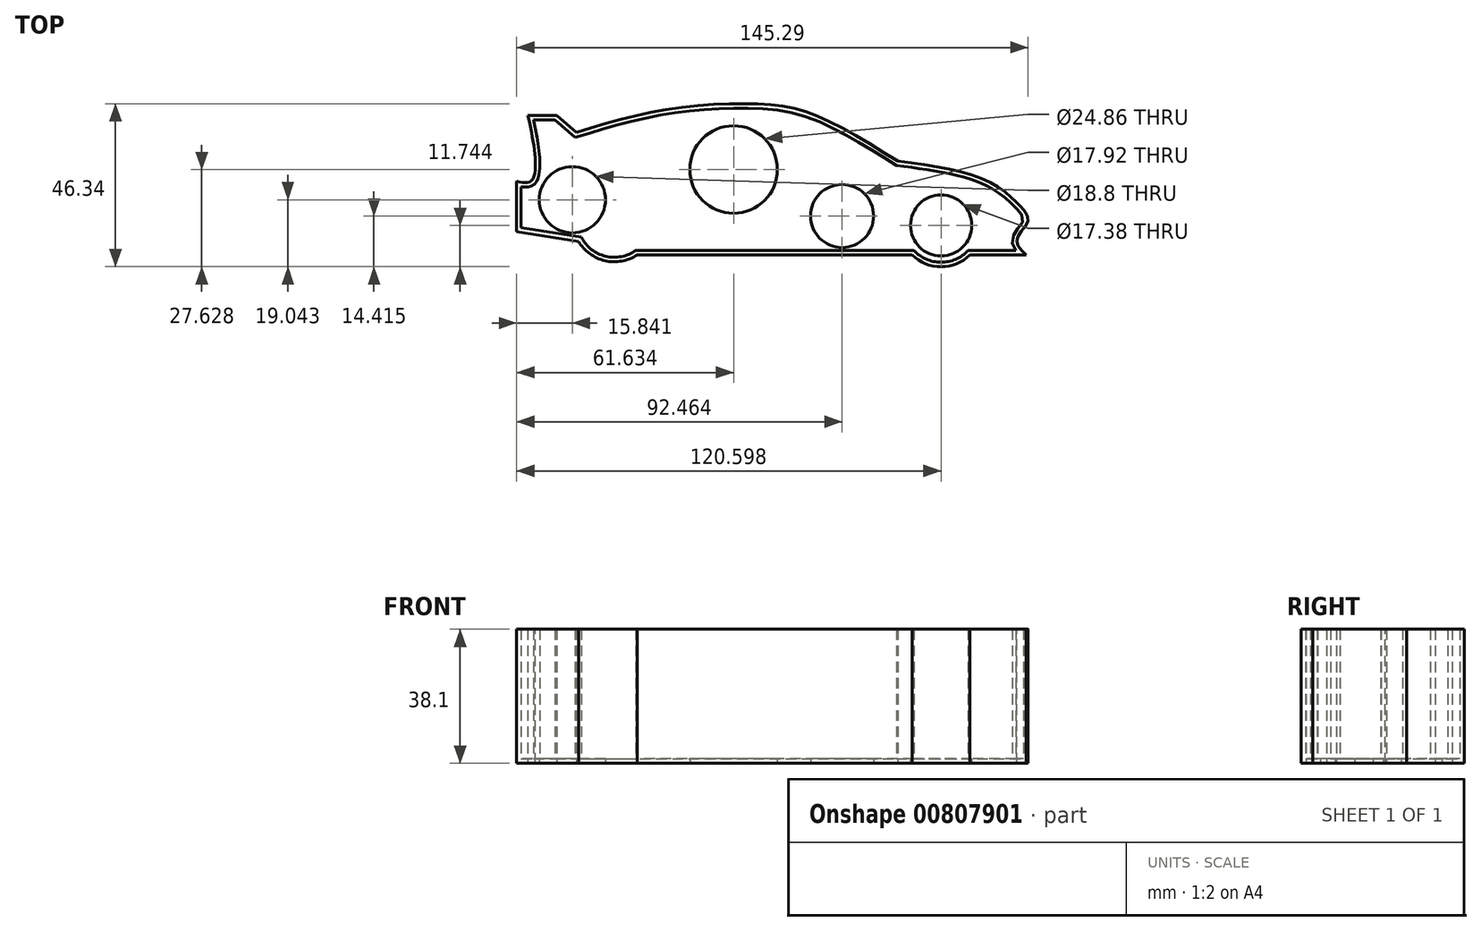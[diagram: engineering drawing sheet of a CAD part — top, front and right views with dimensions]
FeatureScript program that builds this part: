
annotation { "Feature Type Name" : "Feature", "Feature Type Description" : "" }
export const myFeature = defineFeature(function(context is Context, id is Id, definition is map)
    precondition{}
    {
        {
            var Q0;
            Q0=qCreatedBy(makeId("Top.planeOp"),FACE);
            var sketch = newSketch(context, id + "F0", { "sketchPlane" : qUnion([Q0])});
            skFitSpline(sketch, "E0", {"points": [v(35.9, -3.78) * mm, v(61.02, -9.28) * mm, v(70.44, -16.34) * mm, v(72.8, -20.8) * mm, v(69.66, -26.02) * mm, v(72.27, -30.47) * mm], "startDerivative": vector(86.14, -11.78) * mm, "endDerivative": vector(29.8, -29.47) * mm});
            skLineSegment(sketch, "E1", {"start": v(72.27, -30.47) * mm, "end": v(56.34, -30.47) * mm});
            skLineSegment(sketch, "E2", {"start": v(39.86, -30.4) * mm, "end": v(39.86, -30.4) * mm});
            skLineSegment(sketch, "E3", {"start": v(-54.84, -26.57) * mm, "end": v(-72.43, -23.8) * mm});
            skLineSegment(sketch, "E4", {"start": v(-72.43, -23.8) * mm, "end": v(-72.43, -9.5) * mm});
            skFitSpline(sketch, "E5", {"points": [v(-72.43, -9.5) * mm, v(-68.34, -9.5) * mm, v(-67.18, -2.77) * mm, v(-69.22, 9.2) * mm], "startDerivative": vector(18.96, -4.5) * mm, "endDerivative": vector(-6.22, 28.23) * mm});
            skLineSegment(sketch, "E6", {"start": v(-69.22, 9.2) * mm, "end": v(-61.04, 9.2) * mm});
            skLineSegment(sketch, "E7", {"start": v(-61.04, 9.2) * mm, "end": v(-55.49, 4.38) * mm});
            skFitSpline(sketch, "E8", {"points": [v(-55.49, 4.38) * mm, v(-29.5, 10.95) * mm, v(-3.23, 12.41) * mm, v(12.54, 9.2) * mm, v(35.9, -3.78) * mm], "startDerivative": vector(95.2, 28.83) * mm, "endDerivative": vector(93.12, -57.68) * mm});
            skArc(sketch, "E9", {"start": v(-54.84, -26.57) * mm, "mid": v(-47.33, -32.07) * mm, "end": v(-38.17, -30.4) * mm});
            skLineSegment(sketch, "E10", {"start": v(39.92, -30.4) * mm, "end": v(-38.17, -30.4) * mm});
            skArc(sketch, "E11", {"start": v(39.92, -30.4) * mm, "mid": v(48.12, -33.79) * mm, "end": v(56.34, -30.47) * mm});
            skSolve(sketch);
        }
        {
            var Q0;
            Q0=makeQuery(id+"F0.imprint","IMPRINT",FACE,{"disambiguationData":[TD([[makeQuery(id+"F0.imprint","IMPRINT",EDGE,{"derivedFrom":sQuery(id+"F0.wireOp",EDGE,"E0")}),-1.0]])]});
            extrude(context, id + "F1", {"entities" : qUnion([Q0]), "depth" : 38.1 * mm, "offsetDistance" : 25.4 * mm});
        }
        {
            var Q0;
            Q0=makeQuery(id+"F1.opExtrude","CAP_FACE",FACE,{"disambiguationData":[OSD([sQuery(id+"F0.wireOp",EDGE,"E0"),sQuery(id+"F0.wireOp",EDGE,"E1"),sQuery(id+"F0.wireOp",EDGE,"E3"),sQuery(id+"F0.wireOp",EDGE,"E4"),sQuery(id+"F0.wireOp",EDGE,"E5"),sQuery(id+"F0.wireOp",EDGE,"E6"),sQuery(id+"F0.wireOp",EDGE,"E7"),sQuery(id+"F0.wireOp",EDGE,"E8"),sQuery(id+"F0.wireOp",EDGE,"E9"),sQuery(id+"F0.wireOp",EDGE,"E10"),sQuery(id+"F0.wireOp",EDGE,"E11")])],"isStart":false});
            shell(context, id + "F2", {"entities" : qUnion([Q0]), "thickness" : 1.27 * mm});
        }
        {
            var Q0;
            Q0=makeQuery(id+"F1.opExtrude","CAP_FACE",FACE,{"disambiguationData":[OSD([sQuery(id+"F0.wireOp",EDGE,"E0"),sQuery(id+"F0.wireOp",EDGE,"E1"),sQuery(id+"F0.wireOp",EDGE,"E3"),sQuery(id+"F0.wireOp",EDGE,"E4"),sQuery(id+"F0.wireOp",EDGE,"E5"),sQuery(id+"F0.wireOp",EDGE,"E6"),sQuery(id+"F0.wireOp",EDGE,"E7"),sQuery(id+"F0.wireOp",EDGE,"E8"),sQuery(id+"F0.wireOp",EDGE,"E9"),sQuery(id+"F0.wireOp",EDGE,"E10"),sQuery(id+"F0.wireOp",EDGE,"E11")])],"isStart":true});
            var sketch = newSketch(context, id + "F3", { "sketchPlane" : qUnion([Q0])});
            skCircle(sketch, "E12", {"center": v(-10.8, 6.16) * mm, "radius": 12.43 * mm});
            skCircle(sketch, "E13", {"center": v(20.03, 19.37) * mm, "radius": 8.96 * mm});
            skCircle(sketch, "E14", {"center": v(-56.59, 14.75) * mm, "radius": 9.4 * mm});
            skCircle(sketch, "E15", {"center": v(48.17, 22.05) * mm, "radius": 8.7 * mm});
            skSolve(sketch);
        }
        {
            var Q0;
            Q0 = qSketchRegion(id + "F3", true);
            extrude(context, id + "F4", {"entities" : qUnion([Q0]), "operationType" : NewBodyOperationType.REMOVE, "oppositeDirection" : true, "depth" : 25.4 * mm, "offsetDistance" : 25.4 * mm});
        }
    });
